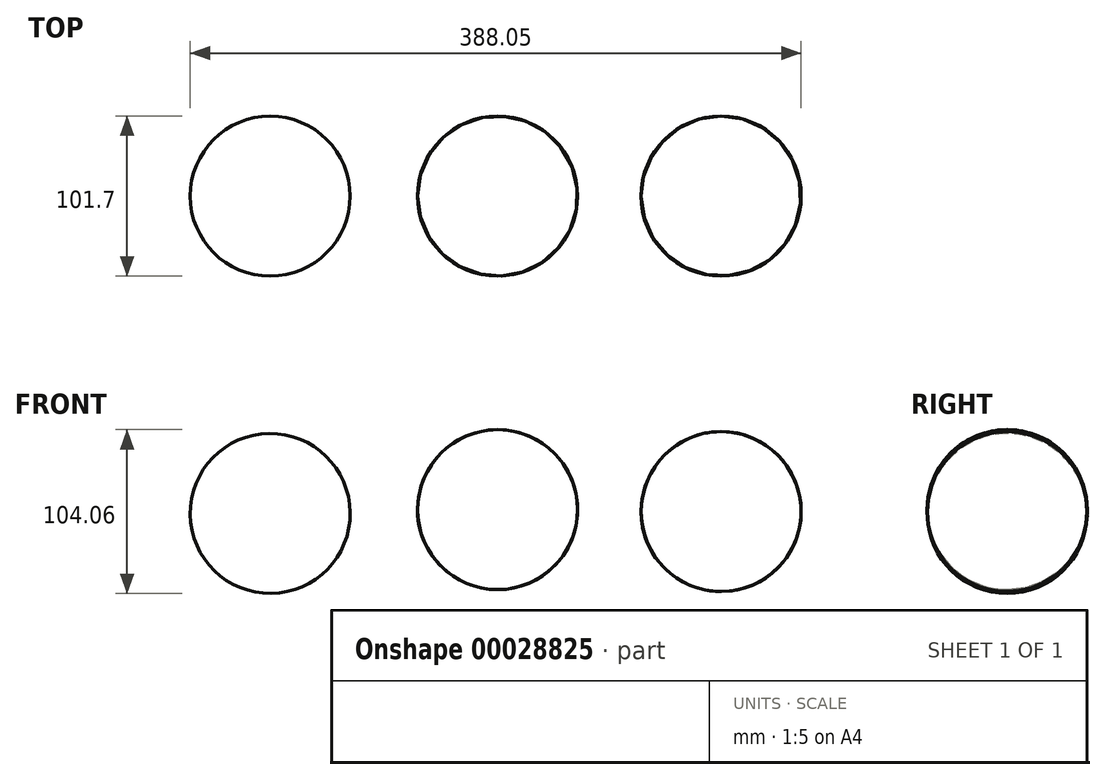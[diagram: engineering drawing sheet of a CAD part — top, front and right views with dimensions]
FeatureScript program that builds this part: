
annotation { "Feature Type Name" : "Feature", "Feature Type Description" : "" }
export const myFeature = defineFeature(function(context is Context, id is Id, definition is map)
    precondition{}
    {
        {
            var Q0;
            Q0=qCreatedBy(makeId("Front.planeOp"),FACE);
            var sketch = newSketch(context, id + "F0", { "sketchPlane" : qUnion([Q0])});
            skArc(sketch, "E0", {"start": v(-15.55, 46.67) * mm, "mid": v(-65.7, -4.77) * mm, "end": v(-14.25, -54.92) * mm});
            skLineSegment(sketch, "E1", {"start": v(-14.25, -54.92) * mm, "end": v(-15.55, 46.67) * mm});
            skSolve(sketch);
        }
        {
            var Q0;
            Q0=makeQuery(id+"F0.imprint","IMPRINT",FACE,{"disambiguationData":[TD([[makeQuery(id+"F0.imprint","IMPRINT",EDGE,{"derivedFrom":sQuery(id+"F0.wireOp",EDGE,"E0")}),1.0]])]});
            var Q1;
            Q1=sQuery(id+"F0.wireOp",EDGE,"E1");
            revolve(context, id + "F1", {"entities" : qUnion([Q0]), "axis" : qUnion([Q1]), "revolveType" : RevolveType.FULL});
        }
        {
            var Q0;
            Q0=qCreatedBy(makeId("Front.planeOp"),FACE);
            var sketch = newSketch(context, id + "F2", { "sketchPlane" : qUnion([Q0])});
            skLineSegment(sketch, "E2", {"start": v(129.53, 49.14) * mm, "end": v(129.53, -52.46) * mm});
            skArc(sketch, "E3", {"start": v(129.53, 49.14) * mm, "mid": v(78.78, -1.66) * mm, "end": v(129.53, -52.46) * mm});
            skSolve(sketch);
        }
        {
            var Q0;
            Q0=makeQuery(id+"F2.imprint","IMPRINT",FACE,{"disambiguationData":[TD([[makeQuery(id+"F2.imprint","IMPRINT",EDGE,{"derivedFrom":sQuery(id+"F2.wireOp",EDGE,"E2")}),-1.0]])]});
            var Q1;
            Q1=sQuery(id+"F2.wireOp",EDGE,"E2");
            revolve(context, id + "F3", {"entities" : qUnion([Q0]), "axis" : qUnion([Q1]), "revolveType" : RevolveType.FULL});
        }
        {
            var Q0;
            Q0=qCreatedBy(makeId("Front.planeOp"),FACE);
            var sketch = newSketch(context, id + "F4", { "sketchPlane" : qUnion([Q0])});
            skLineSegment(sketch, "E4", {"start": v(271.5, 47.9) * mm, "end": v(271.5, -53.7) * mm});
            skArc(sketch, "E5", {"start": v(271.5, 47.9) * mm, "mid": v(220.75, -2.9) * mm, "end": v(271.5, -53.7) * mm});
            skSolve(sketch);
        }
        {
            var Q0;
            Q0=makeQuery(id+"F4.imprint","IMPRINT",FACE,{"disambiguationData":[TD([[makeQuery(id+"F4.imprint","IMPRINT",EDGE,{"derivedFrom":sQuery(id+"F4.wireOp",EDGE,"E4")}),-1.0]])]});
            var Q1;
            Q1=sQuery(id+"F4.wireOp",EDGE,"E4");
            revolve(context, id + "F5", {"entities" : qUnion([Q0]), "axis" : qUnion([Q1]), "revolveType" : RevolveType.FULL});
        }
    });
